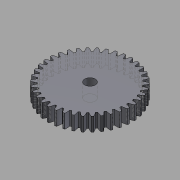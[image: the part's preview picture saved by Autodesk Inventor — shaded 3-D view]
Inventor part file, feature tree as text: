
AUTODESK INVENTOR PART (.ipt)
format: ipt  version: 2015 (Build 190159000, 159)  size: 322,048 bytes
history: native  units: in
note: dims shown in document units (in); Inventor stores cm internally (conversion verified against a paired STEP export)
features: other x13, sketch x3, plane x2
ambient origin geometry x8: Origin, YZ Plane, XZ Plane, XY Plane, X Axis, Y Axis, Z Axis, Center Point
bodies: Solid1 (feature_tree)
feature tree (18):
  other  "Spur Gear2"
  other  "Solid1::Spur Gear2"
  other  "TaggingFeature1"
  sketch  "Sketch1"  dims[d0=0.3937in]
  sketch  "Sketch2"  dims[d16=0.4724in d17=0.0in d41=0.0in d43=0.4724in d46=0.4724in d47=0.0in d48=0.0in]
  sketch  "Sketch3"
  plane  "XZ Plane_1"
  plane  "Work Plane2"
  other  "Z Axis_1"
  other  "Srf1"
  other  "Srf1::Derived"
  other  "Distance iMate"
  other  "Align iMate"
  other  "Mesh iMate"
  other  "Axis iMate"
  other  "Position iMate"
  other  "Mesh iMate2"
  other  "Start plane iMate"
